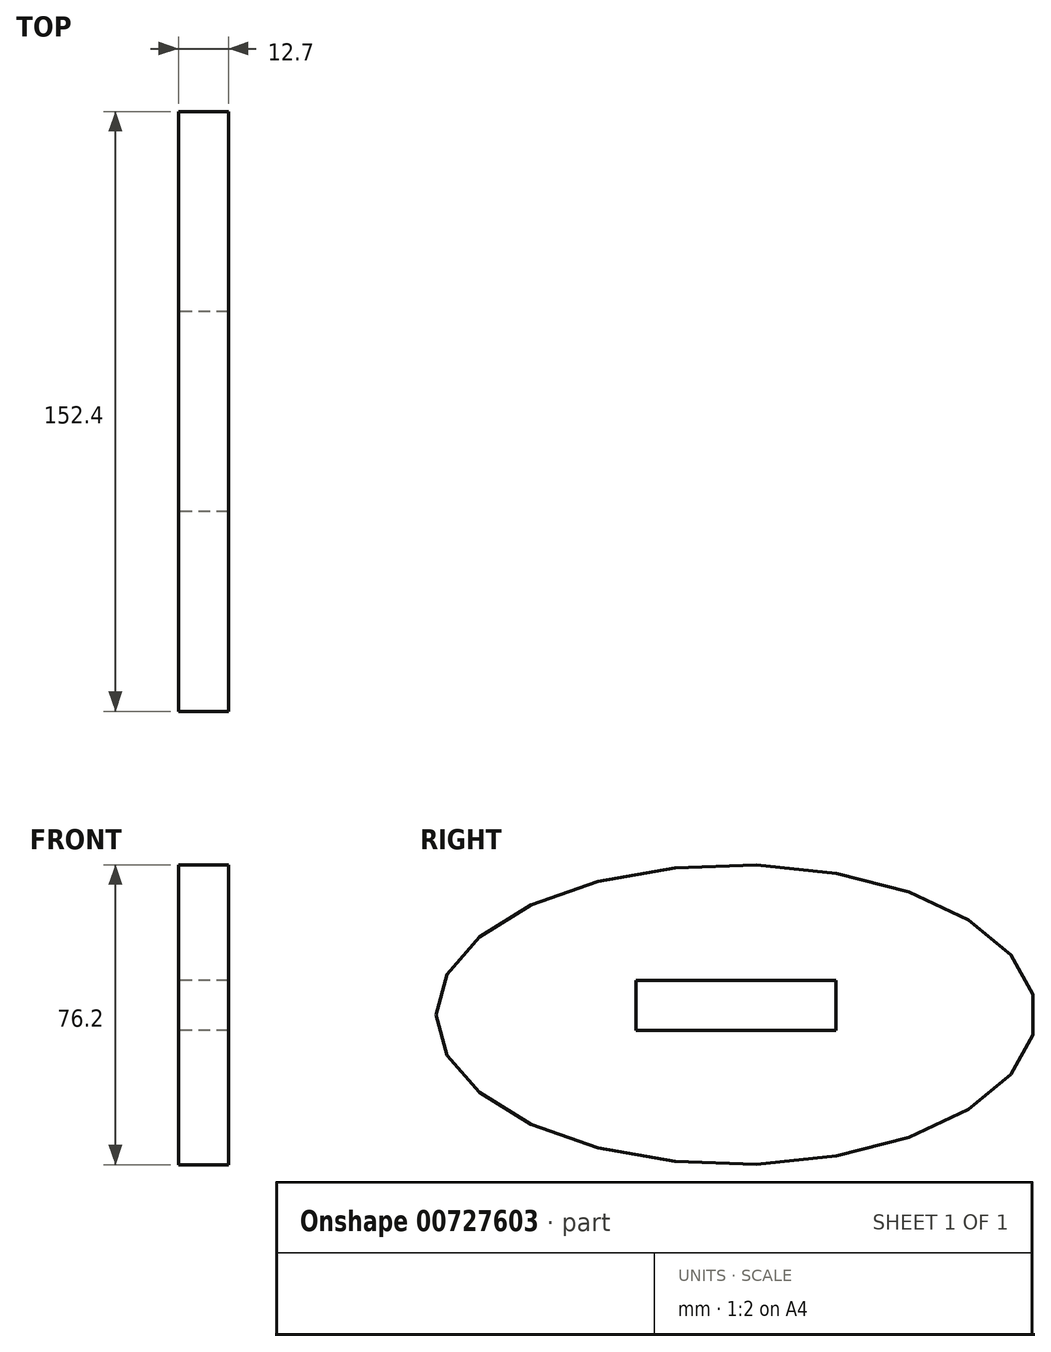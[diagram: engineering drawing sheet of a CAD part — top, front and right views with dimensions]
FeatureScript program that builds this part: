
annotation { "Feature Type Name" : "Feature", "Feature Type Description" : "" }
export const myFeature = defineFeature(function(context is Context, id is Id, definition is map)
    precondition{}
    {
        {
            var Q0;
            Q0=qCreatedBy(makeId("Right.planeOp"),FACE);
            var sketch = newSketch(context, id + "F0", { "sketchPlane" : qUnion([Q0])});
            skEllipse(sketch, "E0", {"center": v(0, -2.42) * mm, "majorRadius": 38.1 * mm, "minorRadius": 76.2 * mm, "majorAxis": v(0, 1)});
            skLineSegment(sketch, "E1.bottom", {"start": v(-25.4, 6.35) * mm, "end": v(25.4, 6.35) * mm});
            skLineSegment(sketch, "E1.top", {"start": v(-25.4, -6.35) * mm, "end": v(25.4, -6.35) * mm});
            skLineSegment(sketch, "E1.left", {"start": v(-25.4, 6.35) * mm, "end": v(-25.4, -6.35) * mm});
            skLineSegment(sketch, "E1.right", {"start": v(25.4, 6.35) * mm, "end": v(25.4, -6.35) * mm});
            skPoint(sketch, "E1.middle", {"position": v(0, 0) * mm});
            skSolve(sketch);
        }
        {
            var Q0;
            Q0=makeQuery(id+"F0.imprint","IMPRINT",FACE,{"disambiguationData":[TD([[makeQuery(id+"F0.imprint","IMPRINT",EDGE,{"derivedFrom":sQuery(id+"F0.wireOp",EDGE,"E0")}),1.0]])]});
            extrude(context, id + "F1", {"entities" : qUnion([Q0]), "depth" : 12.7 * mm, "offsetDistance" : 25.4 * mm});
        }
    });
